# Revit family: ERFP82K
name_source: partatom
category: Plumbing Fixtures
units: mm (PartAtom-declared; Revit-internal decimal feet)

## family parameters
Always vertical = Yes
Cut with Voids When Loaded = No
Part Type = Normal
Room Calculation Point = No
Round Connector Dimension = Use Diameter
Shared = No
Work Plane-Based = No

## types (1)
- ERFP82K
    Activation by = Mechanical Front Bubbler Button
    Approx. Shipping Weight = 34 kg
    Bubbler Style = Flexi-Guard ® Safety Bubbler
    Chilling Capacity = 30 LPH
    Description = Elkay Soft Sides Bi-Level Fountain Non-Filtered Non-Refrigerated
Stainless
    Dimensions (L x W x H) = 502mm x 473mm x 1037mm
    Finish = Stainless Steel
    Installation Location = Indoor
    Manufacturer = ELKAY
    Model = ERFP82K
    Mounting Type = Wall Mount (Inwall Frame/Plate)
    Number of Stations = 1
    Power = 220V/50Hz
    Version = 1.0.0.0

## geometry (parser evidence)
native form markers: Sweep x29
no freeform markers — native parametric forms only
